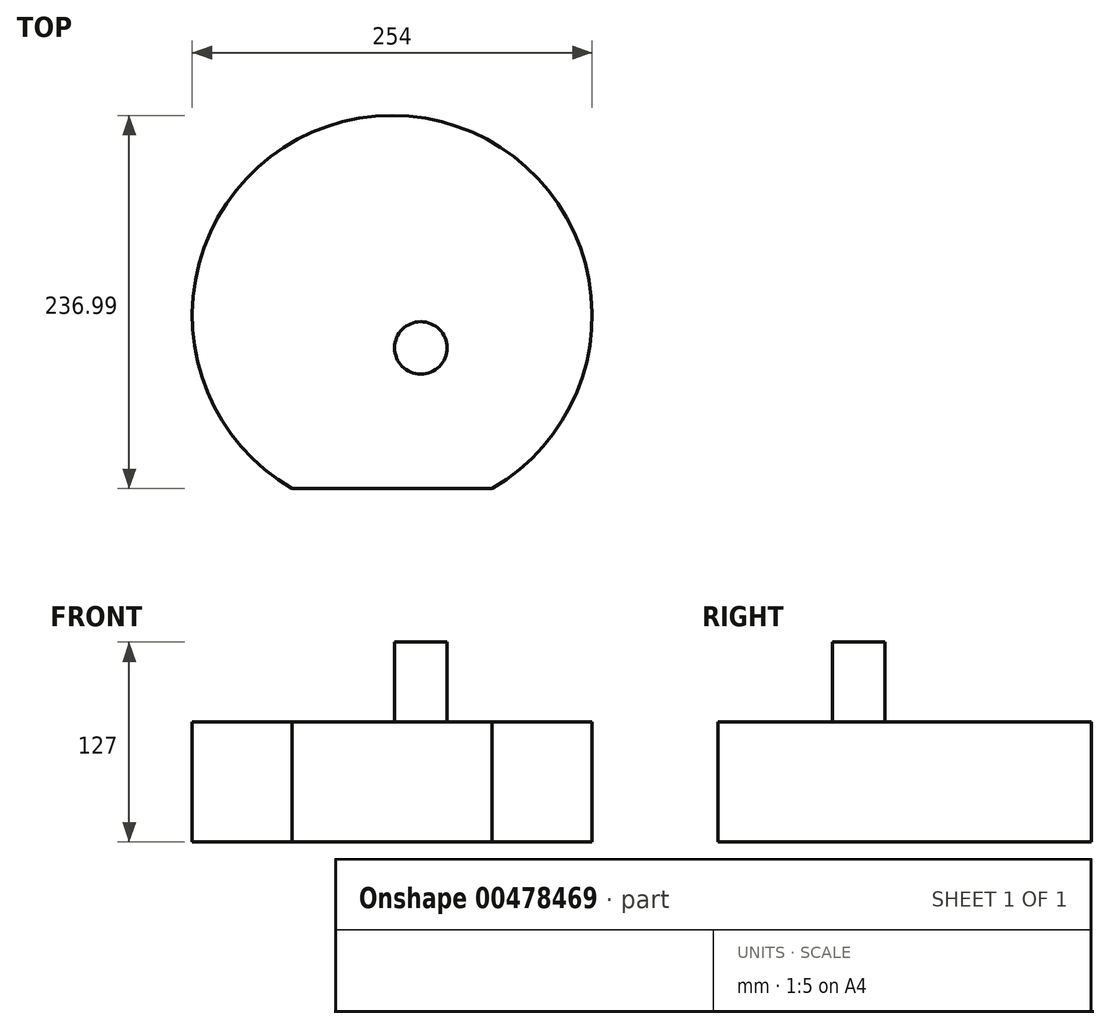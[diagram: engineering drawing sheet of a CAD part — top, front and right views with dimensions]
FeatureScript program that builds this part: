
annotation { "Feature Type Name" : "Feature", "Feature Type Description" : "" }
export const myFeature = defineFeature(function(context is Context, id is Id, definition is map)
    precondition{}
    {
        {
            var Q0;
            Q0=qCreatedBy(makeId("Top.planeOp"),FACE);
            var sketch = newSketch(context, id + "F0", { "sketchPlane" : qUnion([Q0])});
            skLineSegment(sketch, "E0", {"start": v(0, 0) * mm, "end": v(127, 0) * mm});
            skArc(sketch, "E1", {"start": v(127, 0) * mm, "mid": v(63.5, 236.99) * mm, "end": v(0, 0) * mm});
            skCircle(sketch, "E2", {"center": v(63.5, 109.99) * mm, "radius": 59.47 * mm});
            skCircle(sketch, "E3", {"center": v(81.68, 89.35) * mm, "radius": 16.62 * mm});
            skSolve(sketch);
        }
        {
            var Q0;
            Q0=makeQuery(id+"F0.imprint","IMPRINT",FACE,{"disambiguationData":[TD([[makeQuery(id+"F0.imprint","IMPRINT",EDGE,{"derivedFrom":sQuery(id+"F0.wireOp",EDGE,"E3")}),1.0]])]});
            extrude(context, id + "F1", {"entities" : qUnion([Q0]), "depth" : 127 * mm});
        }
        {
            var Q0;
            Q0=makeQuery(id+"F0.imprint","IMPRINT",FACE,{"disambiguationData":[TD([[makeQuery(id+"F0.imprint","IMPRINT",EDGE,{"derivedFrom":sQuery(id+"F0.wireOp",EDGE,"E2")}),1.0]])]});
            extrude(context, id + "F2", {"entities" : qUnion([Q0]), "operationType" : NewBodyOperationType.ADD, "depth" : 76.2 * mm});
        }
        {
            var Q0;
            Q0 = qSketchRegion(id + "F0", true);
            extrude(context, id + "F3", {"entities" : qUnion([Q0]), "operationType" : NewBodyOperationType.ADD, "depth" : 76.2 * mm});
        }
    });
